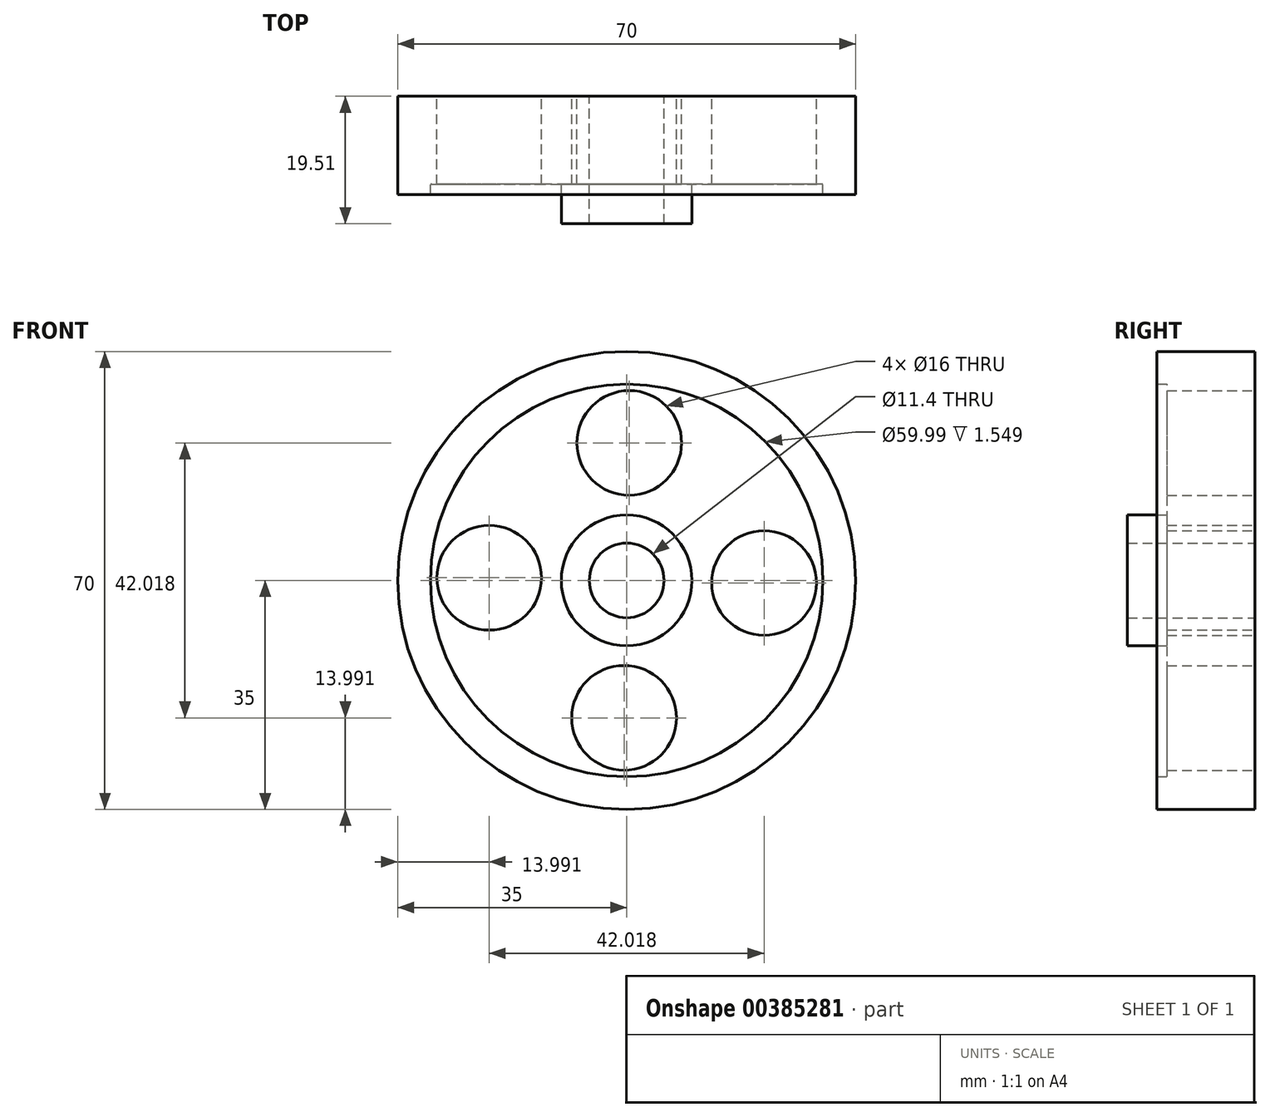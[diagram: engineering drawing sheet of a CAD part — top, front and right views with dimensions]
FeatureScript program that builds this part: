
annotation { "Feature Type Name" : "Feature", "Feature Type Description" : "" }
export const myFeature = defineFeature(function(context is Context, id is Id, definition is map)
    precondition{}
    {
        {
            var Q0;
            Q0=qCreatedBy(makeId("Front.planeOp"),FACE);
            var sketch = newSketch(context, id + "F0", { "sketchPlane" : qUnion([Q0])});
            skCircle(sketch, "E0", {"center": v(0, 0) * mm, "radius": 5.7 * mm});
            skCircle(sketch, "E1", {"center": v(0, 0) * mm, "radius": 10 * mm});
            skPoint(sketch, "E2.0.midPoint", {"position": v(10.7, 10.3) * mm});
            skCircle(sketch, "E3", {"center": v(-21, 0.4) * mm, "radius": 8 * mm});
            skCircle(sketch, "E4", {"center": v(0.4, 21) * mm, "radius": 8 * mm});
            skCircle(sketch, "E5", {"center": v(21, -0.4) * mm, "radius": 8 * mm});
            skCircle(sketch, "E6", {"center": v(-0.4, -21) * mm, "radius": 8 * mm});
            skCircle(sketch, "E7", {"center": v(0, 0) * mm, "radius": 30 * mm});
            skCircle(sketch, "E8", {"center": v(0, 0) * mm, "radius": 35 * mm});
            skSolve(sketch);
        }
        {
            var Q0;
            Q0=makeQuery(id+"F0.imprint","IMPRINT",FACE,{"disambiguationData":[TD([[makeQuery(id+"F0.imprint","IMPRINT",EDGE,{"derivedFrom":sQuery(id+"F0.wireOp",EDGE,"E0")}),-1.0]])]});
            extrude(context, id + "F1", {"entities" : qUnion([Q0]), "depth" : 19.5 * mm});
        }
        {
            var Q0;
            Q0=makeQuery(id+"F0.imprint","IMPRINT",FACE,{"disambiguationData":[TD([[makeQuery(id+"F0.imprint","IMPRINT",EDGE,{"derivedFrom":sQuery(id+"F0.wireOp",EDGE,"E1")}),-1.0]])]});
            extrude(context, id + "F2", {"entities" : qUnion([Q0]), "operationType" : NewBodyOperationType.ADD, "depth" : 13.46 * mm});
        }
        {
            var Q0;
            Q0=makeQuery(id+"F0.imprint","IMPRINT",FACE,{"disambiguationData":[TD([[makeQuery(id+"F0.imprint","IMPRINT",EDGE,{"derivedFrom":sQuery(id+"F0.wireOp",EDGE,"E7")}),-1.0]])]});
            extrude(context, id + "F3", {"entities" : qUnion([Q0]), "operationType" : NewBodyOperationType.ADD, "depth" : 15 * mm});
        }
    });
